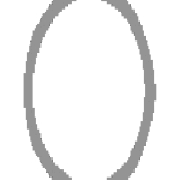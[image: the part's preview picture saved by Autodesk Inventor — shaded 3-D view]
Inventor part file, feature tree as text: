
AUTODESK INVENTOR PART (.ipt)
format: ipt  version: 2021 (Build 250183000, 183)  size: 112,640 bytes
history: native  units: in
note: dims shown in document units (in); Inventor stores cm internally (conversion verified against a paired STEP export)
features: other x4, sketch x3, plane x1
ambient origin geometry x8: Origin, YZ Plane, XZ Plane, XY Plane, X Axis, Y Axis, Z Axis, Center Point
bodies: Solid1 (feature_tree), Body (feature_tree)
feature tree (8):
  other  "Driven Length"
  other  "Frame Generator"
  other  "Start Plane"
  other  "End Plane"
  sketch  "Sketch"  dims[d2=10.9659in d4=-0.0in d5=10.9659in d6=0.12in d7=0.0in d8=90.0deg d9=10.9659in]
  sketch  "Sketch2"  dims[d0=1.0in]
  plane  "Work Plane3"
  sketch  "Sketch3"  dims[d1=0.065in]
